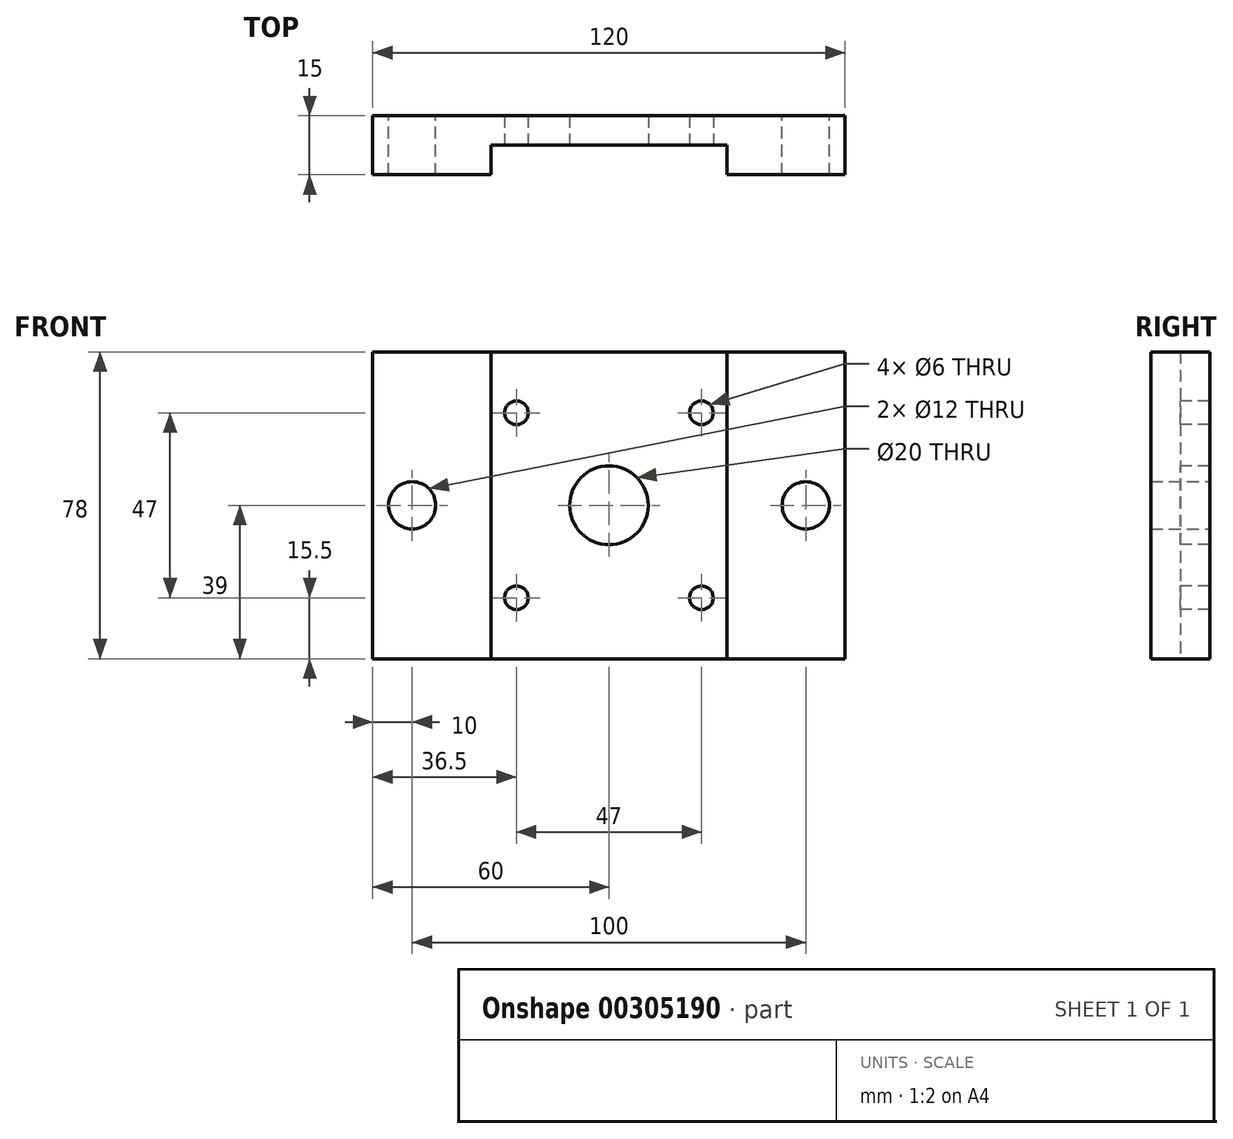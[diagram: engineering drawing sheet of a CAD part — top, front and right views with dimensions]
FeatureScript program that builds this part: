
annotation { "Feature Type Name" : "Feature", "Feature Type Description" : "" }
export const myFeature = defineFeature(function(context is Context, id is Id, definition is map)
    precondition{}
    {
        {
            var Q0;
            Q0=qCreatedBy(makeId("Front.planeOp"),FACE);
            var sketch = newSketch(context, id + "F0", { "sketchPlane" : qUnion([Q0])});
            skLineSegment(sketch, "E0", {"start": v(0, 0) * mm, "end": v(0, 78) * mm});
            skLineSegment(sketch, "E1", {"start": v(0, 78) * mm, "end": v(120, 78) * mm});
            skLineSegment(sketch, "E2", {"start": v(120, 78) * mm, "end": v(120, 0) * mm});
            skLineSegment(sketch, "E3", {"start": v(120, 0) * mm, "end": v(0, 0) * mm});
            skCircle(sketch, "E4", {"center": v(10, 39) * mm, "radius": 6 * mm});
            skPoint(sketch, "E4.centerSnap0", {"position": v(0, 39) * mm});
            skCircle(sketch, "E5", {"center": v(110, 39) * mm, "radius": 6 * mm});
            skSolve(sketch);
        }
        {
            var Q0;
            Q0=makeQuery(id+"F0.imprint","IMPRINT",FACE,{"disambiguationData":[TD([[makeQuery(id+"F0.imprint","IMPRINT",EDGE,{"derivedFrom":sQuery(id+"F0.wireOp",EDGE,"E0")}),-1.0]])]});
            extrude(context, id + "F1", {"entities" : qUnion([Q0]), "depth" : 15 * mm});
        }
        {
            var Q0;
            Q0=makeQuery(id+"F1.opExtrude","CAP_FACE",FACE,{"disambiguationData":[OSD([sQuery(id+"F0.wireOp",EDGE,"E0"),sQuery(id+"F0.wireOp",EDGE,"E1"),sQuery(id+"F0.wireOp",EDGE,"E2"),sQuery(id+"F0.wireOp",EDGE,"E3"),sQuery(id+"F0.wireOp",EDGE,"E4"),sQuery(id+"F0.wireOp",EDGE,"E5")])],"isStart":false});
            var sketch = newSketch(context, id + "F2", { "sketchPlane" : qUnion([Q0])});
            skPoint(sketch, "E6", {"position": v(60, 78) * mm});
            skLineSegment(sketch, "E7", {"start": v(30, 78) * mm, "end": v(30, 0) * mm});
            skLineSegment(sketch, "E8", {"start": v(30, 78) * mm, "end": v(90, 78) * mm});
            skLineSegment(sketch, "E9", {"start": v(90, 78) * mm, "end": v(90, 0) * mm});
            skLineSegment(sketch, "E10", {"start": v(90, 0) * mm, "end": v(30, 0) * mm});
            skSolve(sketch);
        }
        {
            var Q0;
            Q0=makeQuery(id+"F2.imprint","IMPRINT",FACE,{"disambiguationData":[TD([[makeQuery(id+"F2.imprint","IMPRINT",EDGE,{"derivedFrom":sQuery(id+"F2.wireOp",EDGE,"E7")}),1.0]])]});
            extrude(context, id + "F3", {"entities" : qUnion([Q0]), "operationType" : NewBodyOperationType.REMOVE, "oppositeDirection" : true, "depth" : 7.5 * mm});
        }
        {
            var Q0;
            Q0=makeQuery(id+"F3.boolean.opBoolean","COPY",FACE,{"derivedFrom":makeQuery(id+"F3.opExtrude","CAP_FACE",FACE,{"disambiguationData":[OSD([sQuery(id+"F2.wireOp",EDGE,"E7"),sQuery(id+"F2.wireOp",EDGE,"E8"),sQuery(id+"F2.wireOp",EDGE,"E9"),sQuery(id+"F2.wireOp",EDGE,"E10")])],"isStart":false})});
            var sketch = newSketch(context, id + "F4", { "sketchPlane" : qUnion([Q0])});
            skPoint(sketch, "E11", {"position": v(60, 78) * mm});
            skPoint(sketch, "E12", {"position": v(30, 39) * mm});
            skPoint(sketch, "E13", {"position": v(36.5, 62.5) * mm});
            skPoint(sketch, "E14", {"position": v(83.5, 62.5) * mm});
            skPoint(sketch, "E15", {"position": v(83.5, 15.5) * mm});
            skPoint(sketch, "E16", {"position": v(36.5, 15.5) * mm});
            skSolve(sketch);
        }
        {
            var Q0;
            Q0=sQuery(id+"F4.wireOp",VERTEX,"E13");
            var Q1;
            Q1=sQuery(id+"F4.wireOp",VERTEX,"E16");
            var Q2;
            Q2=sQuery(id+"F4.wireOp",VERTEX,"E15");
            var Q3;
            Q3=sQuery(id+"F4.wireOp",VERTEX,"E14");
            var Q4;
            Q4=makeQuery(id+"F1.opExtrude","SWEPT_BODY",BODY,{"disambiguationData":[OSD([sQuery(id+"F0.wireOp",EDGE,"E0"),sQuery(id+"F0.wireOp",EDGE,"E1"),sQuery(id+"F0.wireOp",EDGE,"E2"),sQuery(id+"F0.wireOp",EDGE,"E3"),sQuery(id+"F0.wireOp",EDGE,"E4"),sQuery(id+"F0.wireOp",EDGE,"E5")])]});
            hole(context, id + "F5", {"style" : HoleStyle.SIMPLE, "endStyle" : HoleEndStyle.THROUGH, "holeDiameter" : 6 * mm, "tappedDepth" : 12.6 * mm, "tapClearance" : 3, "startFromSketch" : true, "locations" : qUnion([Q0, Q1, Q2, Q3]), "scope" : qUnion([Q4])});
        }
        {
            var Q0;
            Q0=makeQuery(id+"F3.boolean.opBoolean","COPY",FACE,{"derivedFrom":makeQuery(id+"F3.opExtrude","CAP_FACE",FACE,{"disambiguationData":[OSD([sQuery(id+"F2.wireOp",EDGE,"E7"),sQuery(id+"F2.wireOp",EDGE,"E8"),sQuery(id+"F2.wireOp",EDGE,"E9"),sQuery(id+"F2.wireOp",EDGE,"E10")])],"isStart":false})});
            var sketch = newSketch(context, id + "F6", { "sketchPlane" : qUnion([Q0])});
            skPoint(sketch, "E17", {"position": v(60, 39) * mm});
            skSolve(sketch);
        }
        {
            var Q0;
            Q0=sQuery(id+"F6.wireOp",VERTEX,"E17");
            var Q1;
            Q1=makeQuery(id+"F1.opExtrude","SWEPT_BODY",BODY,{"disambiguationData":[OSD([sQuery(id+"F0.wireOp",EDGE,"E0"),sQuery(id+"F0.wireOp",EDGE,"E1"),sQuery(id+"F0.wireOp",EDGE,"E2"),sQuery(id+"F0.wireOp",EDGE,"E3"),sQuery(id+"F0.wireOp",EDGE,"E4"),sQuery(id+"F0.wireOp",EDGE,"E5")])]});
            hole(context, id + "F7", {"style" : HoleStyle.SIMPLE, "endStyle" : HoleEndStyle.THROUGH, "holeDiameter" : 20 * mm, "tappedDepth" : 12.6 * mm, "tapClearance" : 3, "startFromSketch" : true, "locations" : qUnion([Q0]), "scope" : qUnion([Q1])});
        }
    });
